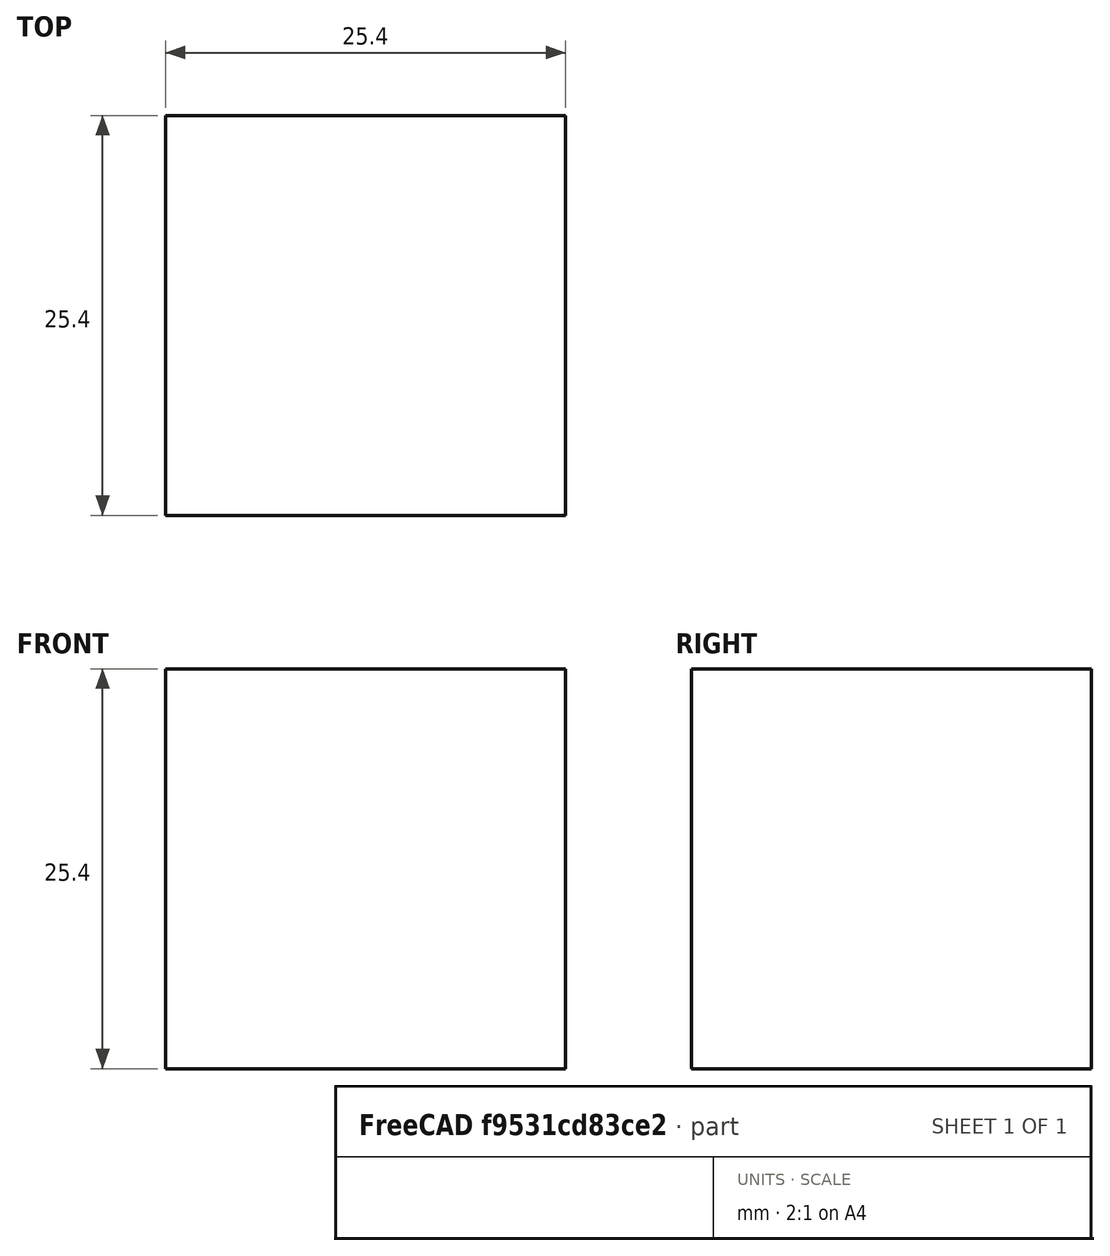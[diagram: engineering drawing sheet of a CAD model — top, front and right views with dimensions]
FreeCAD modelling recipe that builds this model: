
FCSTD DOCUMENT  (FreeCAD 0.22R33992 (Git))
Label: Cube
License: All rights reserved
LicenseURL: http://en.wikipedia.org/wiki/All_rights_reserved
objects: Sketcher::SketchObject×1, PartDesign::Pad×1, PartDesign::Body×1
note: 4 computed .brp shape members not serialized (recipe doc carries the construction recipe); baked Part::Feature solids carry a one-line shape summary decoded from their .brp

FEATURE [Sketcher::SketchObject] Sketch
  FullyConstrained = true
  MapMode = 5
  Support = -> [XY_Plane]
  sketch-geometry (5):
    g0: LineSegment StartX=-12.7 StartY=-12.7 StartZ=0 EndX=-12.7 EndY=12.7 EndZ=0
    g1: LineSegment StartX=-12.7 StartY=12.7 StartZ=0 EndX=12.7 EndY=12.7 EndZ=0
    g2: LineSegment StartX=12.7 StartY=12.7 StartZ=0 EndX=12.7 EndY=-12.7 EndZ=0
    g3: LineSegment StartX=12.7 StartY=-12.7 StartZ=0 EndX=-12.7 EndY=-12.7 EndZ=0
    g4: GeomPoint X=-1e-16 Y=0 Z=0
  constraints (12):
    c: Coincident(g0,g1)
    c: Coincident(g1,g2)
    c: Coincident(g2,g3)
    c: Coincident(g3,g0)
    c: Horizontal(g1)
    c: Horizontal(g3)
    c: Vertical(g0)
    c: Vertical(g2)
    c: Symmetric(g1,g0,g4)
    c: Coincident(g4,g-1)
    c: Equal(g1,g2)
    c: Distance(g2) = 25.4
FEATURE [PartDesign::Pad] Pad
  Direction = (0,0,1)
  Length = 25.4
  Length2 = 10
  Midplane = true
  Profile = -> Sketch
  ReferenceAxis = -> Sketch [N_Axis]
  Type = 0
FEATURE [PartDesign::Body] Body  label="Cube Body"
  Group = -> [Sketch,Pad]
  Origin = -> Origin
  Tip = -> Pad
